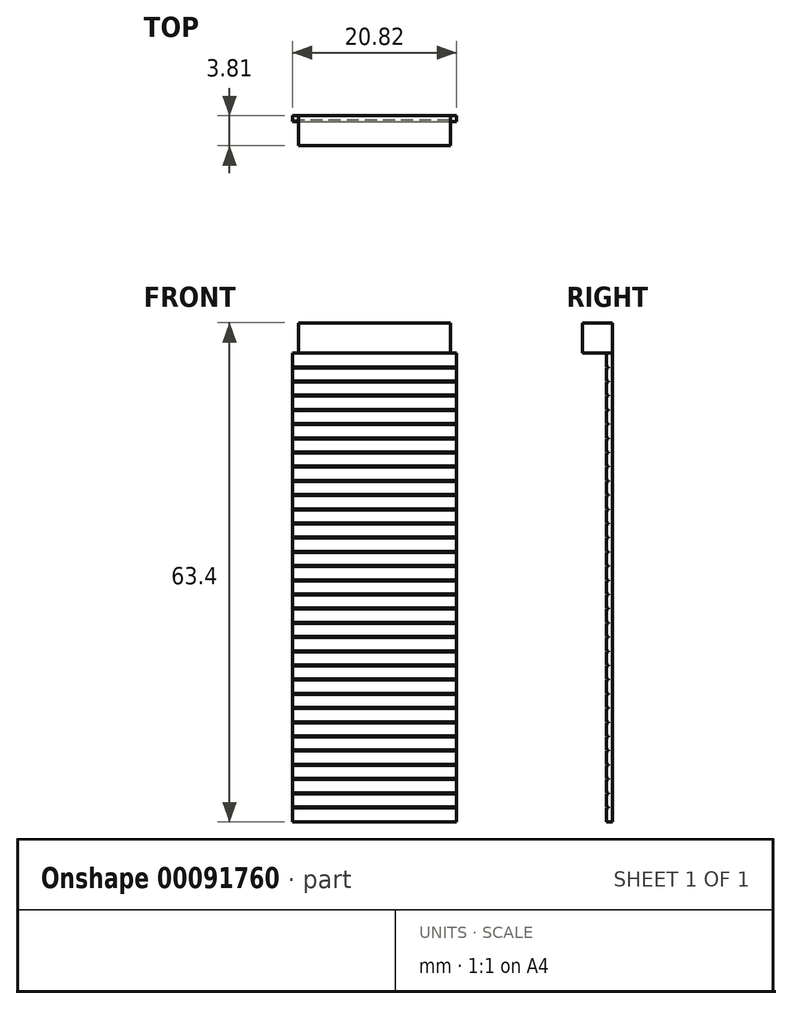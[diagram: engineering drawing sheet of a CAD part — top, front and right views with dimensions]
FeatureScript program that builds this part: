
annotation { "Feature Type Name" : "Feature", "Feature Type Description" : "" }
export const myFeature = defineFeature(function(context is Context, id is Id, definition is map)
    precondition{}
    {
        {
            var Q0;
            Q0=qCreatedBy(makeId("Front.planeOp"),FACE);
            var sketch = newSketch(context, id + "F0", { "sketchPlane" : qUnion([Q0])});
            skLineSegment(sketch, "E0.bottom", {"start": v(-9.65, 59.59) * mm, "end": v(9.65, 59.59) * mm});
            skLineSegment(sketch, "E0.top", {"start": v(-9.65, 0) * mm, "end": v(9.65, 0) * mm});
            skLineSegment(sketch, "E0.left", {"start": v(-9.65, 59.59) * mm, "end": v(-9.65, 0) * mm});
            skLineSegment(sketch, "E0.right", {"start": v(9.65, 59.59) * mm, "end": v(9.65, 0) * mm});
            skSolve(sketch);
        }
        {
            var Q0;
            Q0 = qSketchRegion(id + "F0", true);
            extrude(context, id + "F1", {"entities" : qUnion([Q0]), "depth" : 0.76 * mm});
        }
        {
            var Q0;
            Q0=qCreatedBy(makeId("Front.planeOp"),FACE);
            var sketch = newSketch(context, id + "F2", { "sketchPlane" : qUnion([Q0])});
            skLineSegment(sketch, "E1.bottom", {"start": v(-9.65, 59.59) * mm, "end": v(-10.41, 59.59) * mm});
            skLineSegment(sketch, "E1.top", {"start": v(-9.65, 0) * mm, "end": v(-10.41, 0) * mm});
            skLineSegment(sketch, "E1.left", {"start": v(-9.65, 59.59) * mm, "end": v(-9.65, 0) * mm});
            skLineSegment(sketch, "E1.right", {"start": v(-10.41, 59.59) * mm, "end": v(-10.41, 0) * mm});
            skLineSegment(sketch, "E2.bottom", {"start": v(9.65, 0) * mm, "end": v(10.41, 0) * mm});
            skLineSegment(sketch, "E2.top", {"start": v(9.65, 59.59) * mm, "end": v(10.41, 59.59) * mm});
            skLineSegment(sketch, "E2.left", {"start": v(9.65, 0) * mm, "end": v(9.65, 59.59) * mm});
            skLineSegment(sketch, "E2.right", {"start": v(10.41, 0) * mm, "end": v(10.41, 59.59) * mm});
            skSolve(sketch);
        }
        {
            var Q0;
            Q0 = qSketchRegion(id + "F2", true);
            extrude(context, id + "F3", {"entities" : qUnion([Q0]), "operationType" : NewBodyOperationType.ADD, "depth" : 0.76 * mm});
        }
        {
            var Q0;
            Q0=qCreatedBy(makeId("Front.planeOp"),FACE);
            var sketch = newSketch(context, id + "F4", { "sketchPlane" : qUnion([Q0])});
            skLineSegment(sketch, "E3.bottom", {"start": v(-9.65, 59.59) * mm, "end": v(9.65, 59.59) * mm});
            skLineSegment(sketch, "E3.top", {"start": v(-9.65, 63.4) * mm, "end": v(9.65, 63.4) * mm});
            skLineSegment(sketch, "E3.left", {"start": v(-9.65, 59.59) * mm, "end": v(-9.65, 63.4) * mm});
            skLineSegment(sketch, "E3.right", {"start": v(9.65, 59.59) * mm, "end": v(9.65, 63.4) * mm});
            skSolve(sketch);
        }
        {
            var Q0;
            Q0 = qSketchRegion(id + "F4", true);
            extrude(context, id + "F5", {"entities" : qUnion([Q0]), "operationType" : NewBodyOperationType.ADD, "depth" : 3.8 * mm});
        }
        {
            var Q0;
            Q0=makeQuery(id+"F1.opExtrude","CAP_FACE",FACE,{"disambiguationData":[OSD([sQuery(id+"F0.wireOp",EDGE,"E0.bottom"),sQuery(id+"F0.wireOp",EDGE,"E0.top"),sQuery(id+"F0.wireOp",EDGE,"E0.left"),sQuery(id+"F0.wireOp",EDGE,"E0.right")])],"isStart":false});
            var sketch = newSketch(context, id + "F6", { "sketchPlane" : qUnion([Q0])});
            skLineSegment(sketch, "E4.bottom", {"start": v(-10.41, 1.78) * mm, "end": v(10.41, 1.78) * mm});
            skLineSegment(sketch, "E4.top", {"start": v(-10.41, 1.9) * mm, "end": v(10.41, 1.9) * mm});
            skLineSegment(sketch, "E4.left", {"start": v(-10.41, 1.78) * mm, "end": v(-10.41, 1.9) * mm});
            skLineSegment(sketch, "E4.right", {"start": v(10.41, 1.78) * mm, "end": v(10.41, 1.9) * mm});
            skLineSegment(sketch, "E5.1.0.0", {"start": v(-10.41, 3.7) * mm, "end": v(10.41, 3.7) * mm});
            skLineSegment(sketch, "E5.1.0.1", {"start": v(-10.41, 3.58) * mm, "end": v(10.41, 3.58) * mm});
            skLineSegment(sketch, "E5.1.0.2", {"start": v(-10.41, 3.58) * mm, "end": v(-10.41, 3.7) * mm});
            skLineSegment(sketch, "E5.1.0.3", {"start": v(10.41, 3.58) * mm, "end": v(10.41, 3.7) * mm});
            skLineSegment(sketch, "E5.2.0.0", {"start": v(-10.41, 5.51) * mm, "end": v(10.41, 5.51) * mm});
            skLineSegment(sketch, "E5.2.0.1", {"start": v(-10.41, 5.38) * mm, "end": v(10.41, 5.38) * mm});
            skLineSegment(sketch, "E5.2.0.2", {"start": v(-10.41, 5.38) * mm, "end": v(-10.41, 5.51) * mm});
            skLineSegment(sketch, "E5.2.0.3", {"start": v(10.41, 5.38) * mm, "end": v(10.41, 5.51) * mm});
            skLineSegment(sketch, "E5.3.0.0", {"start": v(-10.41, 7.32) * mm, "end": v(10.41, 7.32) * mm});
            skLineSegment(sketch, "E5.3.0.1", {"start": v(-10.41, 7.19) * mm, "end": v(10.41, 7.19) * mm});
            skLineSegment(sketch, "E5.3.0.2", {"start": v(-10.41, 7.19) * mm, "end": v(-10.41, 7.32) * mm});
            skLineSegment(sketch, "E5.3.0.3", {"start": v(10.41, 7.19) * mm, "end": v(10.41, 7.32) * mm});
            skLineSegment(sketch, "E5.4.0.0", {"start": v(-10.41, 9.12) * mm, "end": v(10.41, 9.12) * mm});
            skLineSegment(sketch, "E5.4.0.1", {"start": v(-10.41, 9) * mm, "end": v(10.41, 9) * mm});
            skLineSegment(sketch, "E5.4.0.2", {"start": v(-10.41, 9) * mm, "end": v(-10.41, 9.12) * mm});
            skLineSegment(sketch, "E5.4.0.3", {"start": v(10.41, 9) * mm, "end": v(10.41, 9.12) * mm});
            skLineSegment(sketch, "E5.5.0.0", {"start": v(-10.41, 10.92) * mm, "end": v(10.41, 10.92) * mm});
            skLineSegment(sketch, "E5.5.0.1", {"start": v(-10.41, 10.8) * mm, "end": v(10.41, 10.8) * mm});
            skLineSegment(sketch, "E5.5.0.2", {"start": v(-10.41, 10.8) * mm, "end": v(-10.41, 10.92) * mm});
            skLineSegment(sketch, "E5.5.0.3", {"start": v(10.41, 10.8) * mm, "end": v(10.41, 10.92) * mm});
            skLineSegment(sketch, "E5.6.0.0", {"start": v(-10.41, 12.73) * mm, "end": v(10.41, 12.73) * mm});
            skLineSegment(sketch, "E5.6.0.1", {"start": v(-10.41, 12.6) * mm, "end": v(10.41, 12.6) * mm});
            skLineSegment(sketch, "E5.6.0.2", {"start": v(-10.41, 12.6) * mm, "end": v(-10.41, 12.73) * mm});
            skLineSegment(sketch, "E5.6.0.3", {"start": v(10.41, 12.6) * mm, "end": v(10.41, 12.73) * mm});
            skLineSegment(sketch, "E5.7.0.0", {"start": v(-10.41, 14.53) * mm, "end": v(10.41, 14.53) * mm});
            skLineSegment(sketch, "E5.7.0.1", {"start": v(-10.41, 14.4) * mm, "end": v(10.41, 14.4) * mm});
            skLineSegment(sketch, "E5.7.0.2", {"start": v(-10.41, 14.4) * mm, "end": v(-10.41, 14.53) * mm});
            skLineSegment(sketch, "E5.7.0.3", {"start": v(10.41, 14.4) * mm, "end": v(10.41, 14.53) * mm});
            skLineSegment(sketch, "E5.8.0.0", {"start": v(-10.41, 16.33) * mm, "end": v(10.41, 16.33) * mm});
            skLineSegment(sketch, "E5.8.0.1", {"start": v(-10.41, 16.2) * mm, "end": v(10.41, 16.2) * mm});
            skLineSegment(sketch, "E5.8.0.2", {"start": v(-10.41, 16.2) * mm, "end": v(-10.41, 16.33) * mm});
            skLineSegment(sketch, "E5.8.0.3", {"start": v(10.41, 16.2) * mm, "end": v(10.41, 16.33) * mm});
            skLineSegment(sketch, "E5.9.0.0", {"start": v(-10.41, 18.14) * mm, "end": v(10.41, 18.14) * mm});
            skLineSegment(sketch, "E5.9.0.1", {"start": v(-10.41, 18) * mm, "end": v(10.41, 18) * mm});
            skLineSegment(sketch, "E5.9.0.2", {"start": v(-10.41, 18) * mm, "end": v(-10.41, 18.14) * mm});
            skLineSegment(sketch, "E5.9.0.3", {"start": v(10.41, 18) * mm, "end": v(10.41, 18.14) * mm});
            skLineSegment(sketch, "E5.10.0.0", {"start": v(-10.41, 19.94) * mm, "end": v(10.41, 19.94) * mm});
            skLineSegment(sketch, "E5.10.0.1", {"start": v(-10.41, 19.81) * mm, "end": v(10.41, 19.81) * mm});
            skLineSegment(sketch, "E5.10.0.2", {"start": v(-10.41, 19.81) * mm, "end": v(-10.41, 19.94) * mm});
            skLineSegment(sketch, "E5.10.0.3", {"start": v(10.41, 19.81) * mm, "end": v(10.41, 19.94) * mm});
            skLineSegment(sketch, "E5.11.0.0", {"start": v(-10.41, 21.74) * mm, "end": v(10.41, 21.74) * mm});
            skLineSegment(sketch, "E5.11.0.1", {"start": v(-10.41, 21.62) * mm, "end": v(10.41, 21.62) * mm});
            skLineSegment(sketch, "E5.11.0.2", {"start": v(-10.41, 21.62) * mm, "end": v(-10.41, 21.74) * mm});
            skLineSegment(sketch, "E5.11.0.3", {"start": v(10.41, 21.62) * mm, "end": v(10.41, 21.74) * mm});
            skLineSegment(sketch, "E5.12.0.0", {"start": v(-10.41, 23.55) * mm, "end": v(10.41, 23.55) * mm});
            skLineSegment(sketch, "E5.12.0.1", {"start": v(-10.41, 23.42) * mm, "end": v(10.41, 23.42) * mm});
            skLineSegment(sketch, "E5.12.0.2", {"start": v(-10.41, 23.42) * mm, "end": v(-10.41, 23.55) * mm});
            skLineSegment(sketch, "E5.12.0.3", {"start": v(10.41, 23.42) * mm, "end": v(10.41, 23.55) * mm});
            skLineSegment(sketch, "E5.13.0.0", {"start": v(-10.41, 25.35) * mm, "end": v(10.41, 25.35) * mm});
            skLineSegment(sketch, "E5.13.0.1", {"start": v(-10.41, 25.22) * mm, "end": v(10.41, 25.22) * mm});
            skLineSegment(sketch, "E5.13.0.2", {"start": v(-10.41, 25.22) * mm, "end": v(-10.41, 25.35) * mm});
            skLineSegment(sketch, "E5.13.0.3", {"start": v(10.41, 25.22) * mm, "end": v(10.41, 25.35) * mm});
            skLineSegment(sketch, "E5.14.0.0", {"start": v(-10.41, 27.15) * mm, "end": v(10.41, 27.15) * mm});
            skLineSegment(sketch, "E5.14.0.1", {"start": v(-10.41, 27.03) * mm, "end": v(10.41, 27.03) * mm});
            skLineSegment(sketch, "E5.14.0.2", {"start": v(-10.41, 27.03) * mm, "end": v(-10.41, 27.15) * mm});
            skLineSegment(sketch, "E5.14.0.3", {"start": v(10.41, 27.03) * mm, "end": v(10.41, 27.15) * mm});
            skLineSegment(sketch, "E5.15.0.0", {"start": v(-10.41, 28.96) * mm, "end": v(10.41, 28.96) * mm});
            skLineSegment(sketch, "E5.15.0.1", {"start": v(-10.41, 28.83) * mm, "end": v(10.41, 28.83) * mm});
            skLineSegment(sketch, "E5.15.0.2", {"start": v(-10.41, 28.83) * mm, "end": v(-10.41, 28.96) * mm});
            skLineSegment(sketch, "E5.15.0.3", {"start": v(10.41, 28.83) * mm, "end": v(10.41, 28.96) * mm});
            skLineSegment(sketch, "E5.16.0.0", {"start": v(-10.41, 30.76) * mm, "end": v(10.41, 30.76) * mm});
            skLineSegment(sketch, "E5.16.0.1", {"start": v(-10.41, 30.63) * mm, "end": v(10.41, 30.63) * mm});
            skLineSegment(sketch, "E5.16.0.2", {"start": v(-10.41, 30.63) * mm, "end": v(-10.41, 30.76) * mm});
            skLineSegment(sketch, "E5.16.0.3", {"start": v(10.41, 30.63) * mm, "end": v(10.41, 30.76) * mm});
            skLineSegment(sketch, "E5.17.0.0", {"start": v(-10.41, 32.56) * mm, "end": v(10.41, 32.56) * mm});
            skLineSegment(sketch, "E5.17.0.1", {"start": v(-10.41, 32.44) * mm, "end": v(10.41, 32.44) * mm});
            skLineSegment(sketch, "E5.17.0.2", {"start": v(-10.41, 32.44) * mm, "end": v(-10.41, 32.56) * mm});
            skLineSegment(sketch, "E5.17.0.3", {"start": v(10.41, 32.44) * mm, "end": v(10.41, 32.56) * mm});
            skLineSegment(sketch, "E5.18.0.0", {"start": v(-10.41, 34.37) * mm, "end": v(10.41, 34.37) * mm});
            skLineSegment(sketch, "E5.18.0.1", {"start": v(-10.41, 34.24) * mm, "end": v(10.41, 34.24) * mm});
            skLineSegment(sketch, "E5.18.0.2", {"start": v(-10.41, 34.24) * mm, "end": v(-10.41, 34.37) * mm});
            skLineSegment(sketch, "E5.18.0.3", {"start": v(10.41, 34.24) * mm, "end": v(10.41, 34.37) * mm});
            skLineSegment(sketch, "E5.19.0.0", {"start": v(-10.41, 36.17) * mm, "end": v(10.41, 36.17) * mm});
            skLineSegment(sketch, "E5.19.0.1", {"start": v(-10.41, 36.04) * mm, "end": v(10.41, 36.04) * mm});
            skLineSegment(sketch, "E5.19.0.2", {"start": v(-10.41, 36.04) * mm, "end": v(-10.41, 36.17) * mm});
            skLineSegment(sketch, "E5.19.0.3", {"start": v(10.41, 36.04) * mm, "end": v(10.41, 36.17) * mm});
            skLineSegment(sketch, "E5.20.0.0", {"start": v(-10.41, 37.97) * mm, "end": v(10.41, 37.97) * mm});
            skLineSegment(sketch, "E5.20.0.1", {"start": v(-10.41, 37.85) * mm, "end": v(10.41, 37.85) * mm});
            skLineSegment(sketch, "E5.20.0.2", {"start": v(-10.41, 37.85) * mm, "end": v(-10.41, 37.97) * mm});
            skLineSegment(sketch, "E5.20.0.3", {"start": v(10.41, 37.85) * mm, "end": v(10.41, 37.97) * mm});
            skLineSegment(sketch, "E5.21.0.0", {"start": v(-10.41, 39.78) * mm, "end": v(10.41, 39.78) * mm});
            skLineSegment(sketch, "E5.21.0.1", {"start": v(-10.41, 39.65) * mm, "end": v(10.41, 39.65) * mm});
            skLineSegment(sketch, "E5.21.0.2", {"start": v(-10.41, 39.65) * mm, "end": v(-10.41, 39.78) * mm});
            skLineSegment(sketch, "E5.21.0.3", {"start": v(10.41, 39.65) * mm, "end": v(10.41, 39.78) * mm});
            skLineSegment(sketch, "E5.22.0.0", {"start": v(-10.41, 41.58) * mm, "end": v(10.41, 41.58) * mm});
            skLineSegment(sketch, "E5.22.0.1", {"start": v(-10.41, 41.45) * mm, "end": v(10.41, 41.45) * mm});
            skLineSegment(sketch, "E5.22.0.2", {"start": v(-10.41, 41.45) * mm, "end": v(-10.41, 41.58) * mm});
            skLineSegment(sketch, "E5.22.0.3", {"start": v(10.41, 41.45) * mm, "end": v(10.41, 41.58) * mm});
            skLineSegment(sketch, "E5.23.0.0", {"start": v(-10.41, 43.38) * mm, "end": v(10.41, 43.38) * mm});
            skLineSegment(sketch, "E5.23.0.1", {"start": v(-10.41, 43.26) * mm, "end": v(10.41, 43.26) * mm});
            skLineSegment(sketch, "E5.23.0.2", {"start": v(-10.41, 43.26) * mm, "end": v(-10.41, 43.38) * mm});
            skLineSegment(sketch, "E5.23.0.3", {"start": v(10.41, 43.26) * mm, "end": v(10.41, 43.38) * mm});
            skLineSegment(sketch, "E5.24.0.0", {"start": v(-10.41, 45.19) * mm, "end": v(10.41, 45.19) * mm});
            skLineSegment(sketch, "E5.24.0.1", {"start": v(-10.41, 45.06) * mm, "end": v(10.41, 45.06) * mm});
            skLineSegment(sketch, "E5.24.0.2", {"start": v(-10.41, 45.06) * mm, "end": v(-10.41, 45.19) * mm});
            skLineSegment(sketch, "E5.24.0.3", {"start": v(10.41, 45.06) * mm, "end": v(10.41, 45.19) * mm});
            skLineSegment(sketch, "E5.25.0.0", {"start": v(-10.41, 47) * mm, "end": v(10.41, 47) * mm});
            skLineSegment(sketch, "E5.25.0.1", {"start": v(-10.41, 46.86) * mm, "end": v(10.41, 46.86) * mm});
            skLineSegment(sketch, "E5.25.0.2", {"start": v(-10.41, 46.86) * mm, "end": v(-10.41, 47) * mm});
            skLineSegment(sketch, "E5.25.0.3", {"start": v(10.41, 46.86) * mm, "end": v(10.41, 47) * mm});
            skLineSegment(sketch, "E5.26.0.0", {"start": v(-10.41, 48.8) * mm, "end": v(10.41, 48.8) * mm});
            skLineSegment(sketch, "E5.26.0.1", {"start": v(-10.41, 48.67) * mm, "end": v(10.41, 48.67) * mm});
            skLineSegment(sketch, "E5.26.0.2", {"start": v(-10.41, 48.67) * mm, "end": v(-10.41, 48.8) * mm});
            skLineSegment(sketch, "E5.26.0.3", {"start": v(10.41, 48.67) * mm, "end": v(10.41, 48.8) * mm});
            skLineSegment(sketch, "E5.27.0.0", {"start": v(-10.41, 50.6) * mm, "end": v(10.41, 50.6) * mm});
            skLineSegment(sketch, "E5.27.0.1", {"start": v(-10.41, 50.47) * mm, "end": v(10.41, 50.47) * mm});
            skLineSegment(sketch, "E5.27.0.2", {"start": v(-10.41, 50.47) * mm, "end": v(-10.41, 50.6) * mm});
            skLineSegment(sketch, "E5.27.0.3", {"start": v(10.41, 50.47) * mm, "end": v(10.41, 50.6) * mm});
            skLineSegment(sketch, "E5.28.0.0", {"start": v(-10.41, 52.4) * mm, "end": v(10.41, 52.4) * mm});
            skLineSegment(sketch, "E5.28.0.1", {"start": v(-10.41, 52.27) * mm, "end": v(10.41, 52.27) * mm});
            skLineSegment(sketch, "E5.28.0.2", {"start": v(-10.41, 52.27) * mm, "end": v(-10.41, 52.4) * mm});
            skLineSegment(sketch, "E5.28.0.3", {"start": v(10.41, 52.27) * mm, "end": v(10.41, 52.4) * mm});
            skLineSegment(sketch, "E5.29.0.0", {"start": v(-10.41, 54.2) * mm, "end": v(10.41, 54.2) * mm});
            skLineSegment(sketch, "E5.29.0.1", {"start": v(-10.41, 54.08) * mm, "end": v(10.41, 54.08) * mm});
            skLineSegment(sketch, "E5.29.0.2", {"start": v(-10.41, 54.08) * mm, "end": v(-10.41, 54.2) * mm});
            skLineSegment(sketch, "E5.29.0.3", {"start": v(10.41, 54.08) * mm, "end": v(10.41, 54.2) * mm});
            skLineSegment(sketch, "E5.30.0.0", {"start": v(-10.41, 56) * mm, "end": v(10.41, 56) * mm});
            skLineSegment(sketch, "E5.30.0.1", {"start": v(-10.41, 55.88) * mm, "end": v(10.41, 55.88) * mm});
            skLineSegment(sketch, "E5.30.0.2", {"start": v(-10.41, 55.88) * mm, "end": v(-10.41, 56) * mm});
            skLineSegment(sketch, "E5.30.0.3", {"start": v(10.41, 55.88) * mm, "end": v(10.41, 56) * mm});
            skLineSegment(sketch, "E5.31.0.0", {"start": v(-10.41, 57.81) * mm, "end": v(10.41, 57.81) * mm});
            skLineSegment(sketch, "E5.31.0.1", {"start": v(-10.41, 57.68) * mm, "end": v(10.41, 57.68) * mm});
            skLineSegment(sketch, "E5.31.0.2", {"start": v(-10.41, 57.68) * mm, "end": v(-10.41, 57.81) * mm});
            skLineSegment(sketch, "E5.31.0.3", {"start": v(10.41, 57.68) * mm, "end": v(10.41, 57.81) * mm});
            skLineSegment(sketch, "E5.direction1", {"start": v(-10.41, 1.9) * mm, "end": v(-10.41, 3.7) * mm, "construction": true});
            skSolve(sketch);
        }
        {
            var Q0;
            Q0 = qSketchRegion(id + "F6", true);
            extrude(context, id + "F7", {"entities" : qUnion([Q0]), "operationType" : NewBodyOperationType.REMOVE, "oppositeDirection" : true, "depth" : 0.25 * mm});
        }
    });
